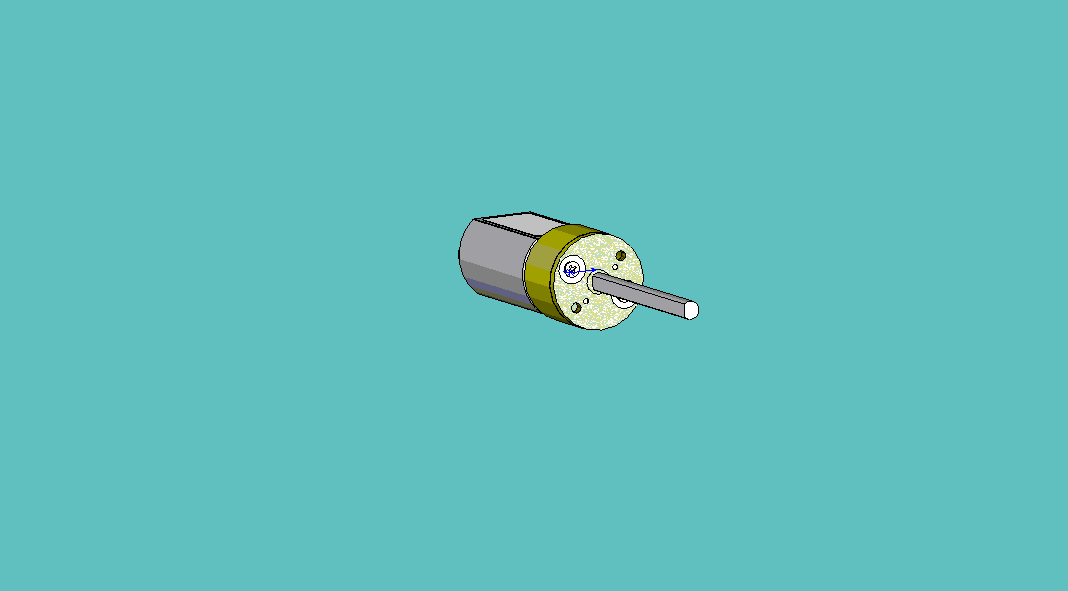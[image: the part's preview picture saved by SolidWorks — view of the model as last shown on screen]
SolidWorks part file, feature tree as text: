
SOLIDWORKS PART (.sldprt)
format: sldprt  version: not decoded by parser v0  size: 905,216 bytes
history: native  units: mm
features: sketch x16, extrude x11, cut_extrude x5, fillet x4, chamfer x2, material x1 (+13 scaffold rows collapsed)
feature tree (52):
  scaffold x13  (default folders/planes/origin — collapsed)
  material  "Material <not specified>"
  sketch  "Sketch2"  dims[D2=15.5mm D1=12.0mm]
  extrude  "Extrude2"  Depth=26.6954mm
  fillet  "Fillet1"  Radius=0.254mm
  fillet  "Fillet2"  Radius=0.762mm
  sketch  "Sketch6"  dims[c1.D1=~14.280824mm c1.D4=8.9154mm c1.D5=2.1844mm c1.D7=~7.034903mm c1.D8=7.1232mm c2.D1=0.4445mm c2.D2=0.4445mm c2.D3=0.4445mm c2.D6=8.9154mm c3.D6=~42.464938deg c4.D6=6.8326mm c4.D7=3.7465mm c4.D8=2.1082mm]
  cut_extrude  "Cut-Extrude2"  Depth=0.5461mm
  fillet  "Fillet4"  Radius=0.2032mm
  sketch  "Sketch7"  dims[D1=4.7mm]
  extrude  "Extrude5"  Depth=1.9mm
  fillet  "Fillet3"  Radius=0.508mm
  sketch  "Sketch8"  dims[D1=2.0mm D2=0.3mm D3=12.1mm]
  extrude  "Extrude6"  Depth=3.6mm
  chamfer  "Chamfer1"  Distance=0.508mm Angle=45deg
  sketch  "Sketch9"  dims[D1=1.1mm D2=1.1mm]
  cut_extrude  "Cut-Extrude3"  [1 undecoded]
  sketch  "Sketch10"  dims[D1=1.1mm D2=1.1mm]
  cut_extrude  "Cut-Extrude4"  [1 undecoded]
  sketch  "Sketch11"  dims[D1=6.0mm]
  extrude  "Extrude7"  Depth=1.5mm
  sketch  "Sketch1"  dims[D1=15.58mm D2=0.7343mm]
  extrude  "Extrude1"  Depth=10.3mm
  sketch  "Sketch12"  dims[D1=15.45mm]
  extrude  "Extrude8"  Depth=1.5mm
  sketch  "Sketch3"  dims[D1=3.9878mm]
  extrude  "Extrude3"  Depth=0.01mm
  sketch  "Sketch4"  dims[D1=2.98mm D2=2.49mm]
  extrude  "Extrude4"  Depth=37.5mm
  sketch  "Sketch5"  dims[c1.D1=1.651mm c1.D6=0.9mm c1.D2=10.0mm c1.D3=11.0mm c1.D4=11.0mm c2.D4=45.0deg c2.D5=~8.160245mm c3.D5=30.0deg c3.D4=6.2mm c3.D7=~0.55714mm c3.D8=7.2mm]
  cut_extrude  "Cut-Extrude1"  [1 undecoded]
  chamfer  "Chamfer2"  Distance=0.6mm
  sketch  "Sketch13"  dims[D1=2.5mm]
  extrude  "Extrude11"  Depth=0.4064mm
  sketch  "Sketch14"  dims[D1=0.35mm D2=1.4mm]
  cut_extrude  "Cut-Extrude5"  Depth=0.254mm
  sketch  "Sketch15"  dims[D1=0.8mm]
  extrude  "Extrude12"  Depth=1.27mm
  sketch  "Sketch16"  dims[D3=1.4mm D1=23.7mm D2=8.4mm]
  extrude  "Extrude13"  Depth=0.1mm
decode coverage: 35 of 38 modeling features carry decoded parameters
note: ~ marks probable driven/reference dimensions
note: 3 parameter values undecoded
summary: no parameter record found for 3 features
note: suppression state not decoded; provenance and decode notes live in map.json
